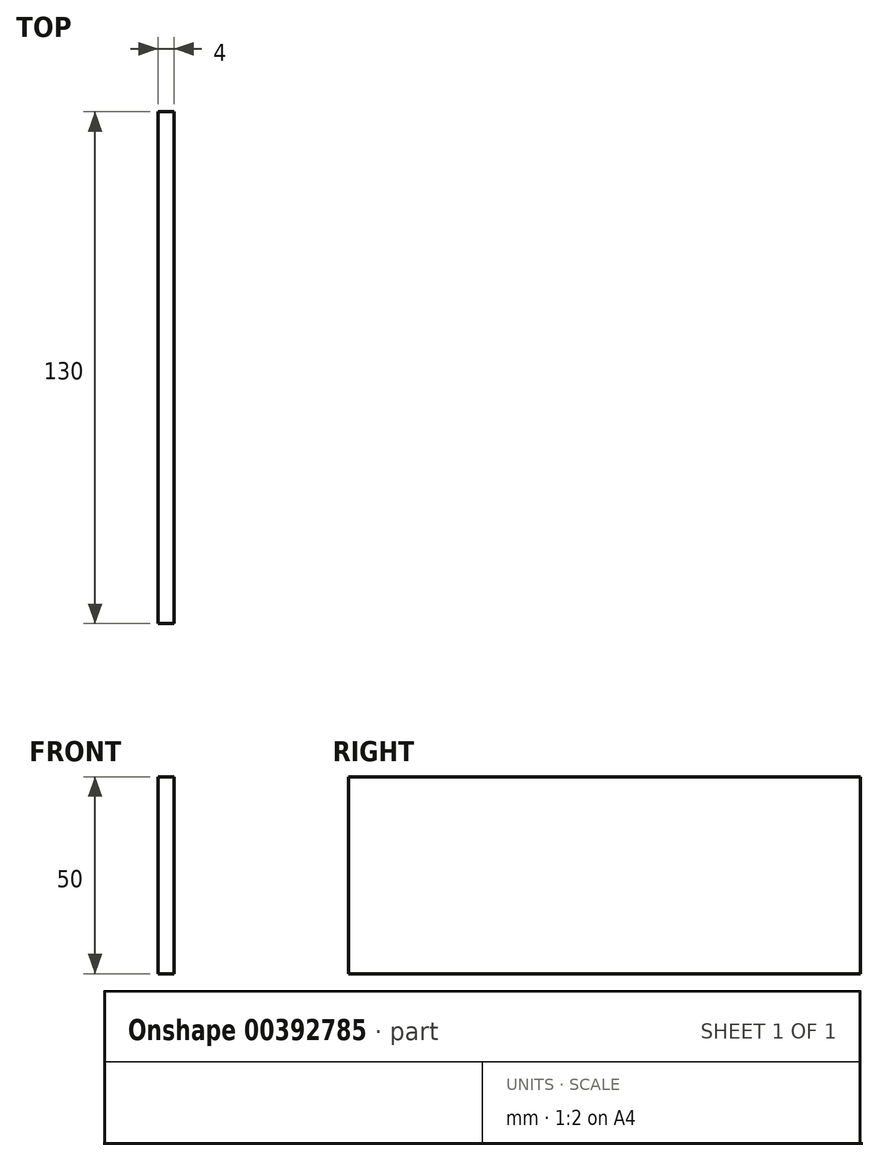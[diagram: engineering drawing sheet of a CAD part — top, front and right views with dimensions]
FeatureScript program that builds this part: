
annotation { "Feature Type Name" : "Feature", "Feature Type Description" : "" }
export const myFeature = defineFeature(function(context is Context, id is Id, definition is map)
    precondition{}
    {
        {
            var Q0;
            Q0=qCreatedBy(makeId("Top.planeOp"),FACE);
            var sketch = newSketch(context, id + "F0", { "sketchPlane" : qUnion([Q0])});
            skLineSegment(sketch, "E0.bottom", {"start": v(0, 0) * mm, "end": v(4, 0) * mm});
            skLineSegment(sketch, "E0.top", {"start": v(0, 130) * mm, "end": v(4, 130) * mm});
            skLineSegment(sketch, "E0.left", {"start": v(0, 0) * mm, "end": v(0, 130) * mm});
            skLineSegment(sketch, "E0.right", {"start": v(4, 0) * mm, "end": v(4, 130) * mm});
            skSolve(sketch);
        }
        {
            var Q0;
            Q0 = qSketchRegion(id + "F0", true);
            extrude(context, id + "F1", {"entities" : qUnion([Q0]), "depth" : 50 * mm});
        }
    });
